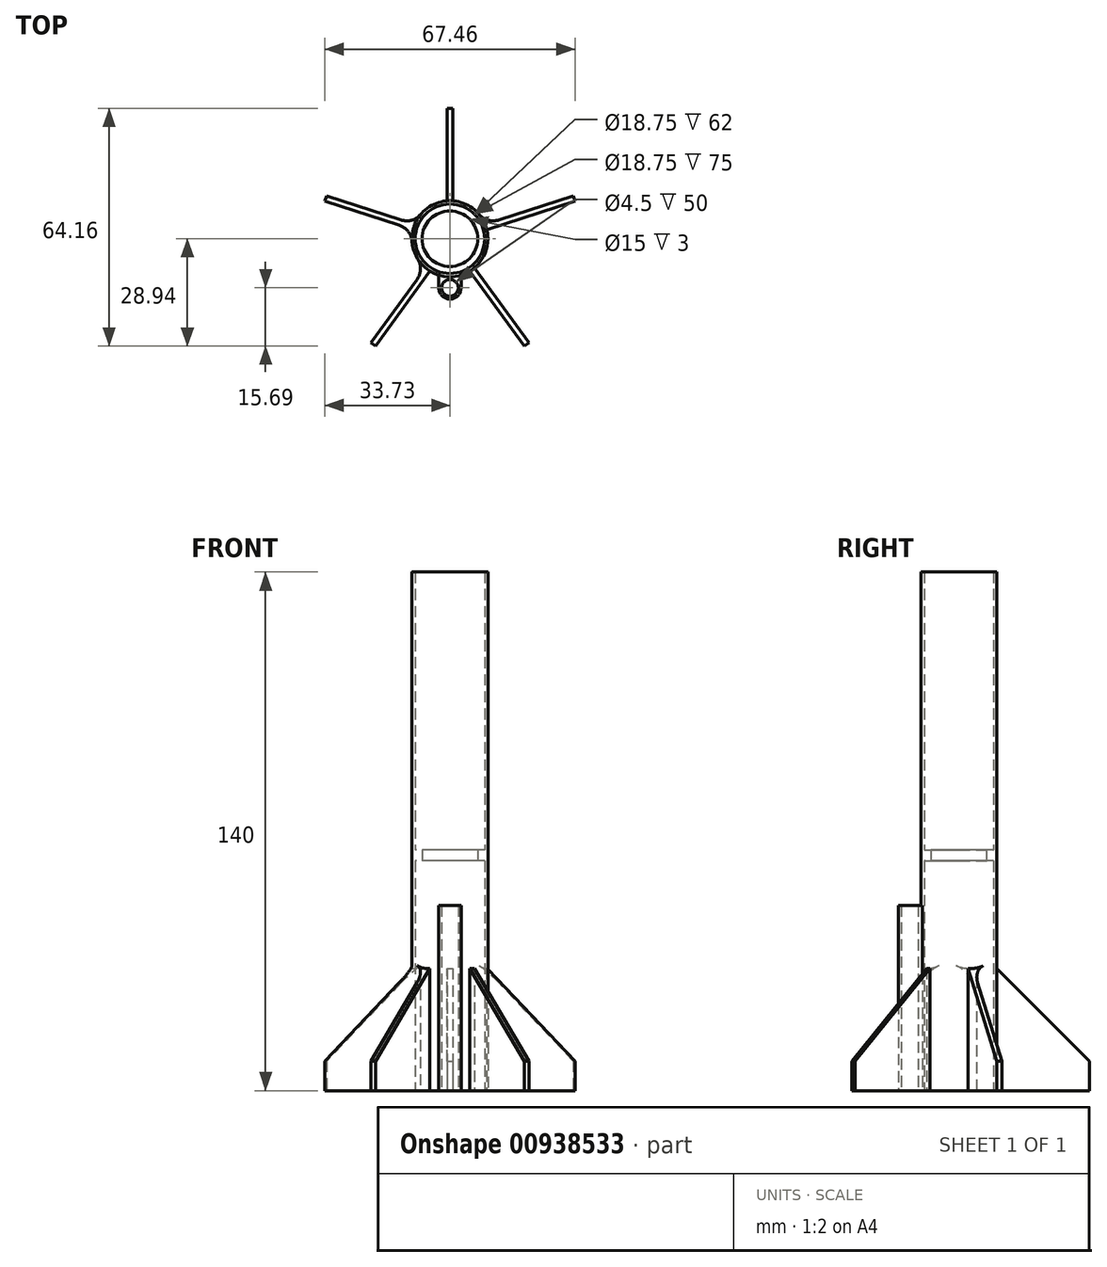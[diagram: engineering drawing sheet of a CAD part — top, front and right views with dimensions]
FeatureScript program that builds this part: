
annotation { "Feature Type Name" : "Feature", "Feature Type Description" : "" }
export const myFeature = defineFeature(function(context is Context, id is Id, definition is map)
    precondition{}
    {
        {
            var Q0;
            Q0=qCreatedBy(makeId("Top.planeOp"),FACE);
            var sketch = newSketch(context, id + "F0", { "sketchPlane" : qUnion([Q0])});
            skCircle(sketch, "E0", {"center": v(0, 0) * mm, "radius": 10.25 * mm});
            skCircle(sketch, "E1", {"center": v(0, 0) * mm, "radius": 9.38 * mm});
            skCircle(sketch, "E2", {"center": v(0, -13.25) * mm, "radius": 3 * mm});
            skCircle(sketch, "E3", {"center": v(0, -13.25) * mm, "radius": 2.25 * mm});
            skLineSegment(sketch, "E4", {"start": v(-3, -9.8) * mm, "end": v(-3, -13.25) * mm});
            skLineSegment(sketch, "E5.MirrorCS", {"start": v(3, -9.8) * mm, "end": v(3, -13.25) * mm});
            skLineSegment(sketch, "E6.bottom", {"start": v(-0.75, 35.22) * mm, "end": v(0.75, 35.22) * mm});
            skLineSegment(sketch, "E6.top", {"start": v(-0.75, 10.22) * mm, "end": v(0.75, 10.22) * mm, "construction": true});
            skLineSegment(sketch, "E6.left", {"start": v(-0.75, 35.22) * mm, "end": v(-0.75, 10.22) * mm});
            skLineSegment(sketch, "E6.right", {"start": v(0.75, 35.22) * mm, "end": v(0.75, 10.22) * mm});
            skCircle(sketch, "E7", {"center": v(0, 0) * mm, "radius": 7.5 * mm});
            skSolve(sketch);
        }
        {
            var Q0;
            Q0=makeQuery(id+"F0.imprint","IMPRINT",FACE,{"disambiguationData":[TD([[makeQuery(id+"F0.imprint","IMPRINT",EDGE,{"derivedFrom":sQuery(id+"F0.wireOp",EDGE,"E1")}),-1.0]])]});
            extrude(context, id + "F1", {"entities" : qUnion([Q0]), "depth" : 140 * mm, "offsetDistance" : 25 * mm});
        }
        {
            var Q0;
            Q0=makeQuery(id+"F0.imprint","IMPRINT",FACE,{"disambiguationData":[TD([[makeQuery(id+"F0.imprint","IMPRINT",EDGE,{"derivedFrom":sQuery(id+"F0.wireOp",EDGE,"E6.bottom")}),-1.0]])]});
            extrude(context, id + "F2", {"entities" : qUnion([Q0]), "operationType" : NewBodyOperationType.ADD, "depth" : 48 * mm, "offsetDistance" : 25 * mm});
        }
        {
            var Q0;
            Q0=makeQuery(id+"F2.opExtrude","CAP_EDGE",EDGE,{"disambiguationData":[OSD([sQuery(id+"F0.wireOp",EDGE,"E6.bottom")])],"isStart":false});
            chamfer(context, id + "F3", {"entities" : qUnion([Q0]), "width" : 40 * mm, "tangentPropagation" : true});
        }
        {
            var Q0;
            Q0=makeQuery(id+"F1.opExtrude","SWEPT_BODY",BODY,{"disambiguationData":[OSD([sQuery(id+"F0.wireOp",EDGE,"E0"),sQuery(id+"F0.wireOp",EDGE,"E1")])]});
            var Q1;
            Q1=sQuery(id+"F0.wireOp",EDGE,"E0");
            circularPattern(context, id + "F4", {"operationType" : NewBodyOperationType.ADD, "entities" : qUnion([Q0]), "axis" : qUnion([Q1]), "angle" : 360 * degree, "instanceCount" : 5, "equalSpace" : true});
        }
        {
            var Q0;
            Q0=makeQuery(id+"F0.imprint","IMPRINT",FACE,{"disambiguationData":[TD([[makeQuery(id+"F0.imprint","IMPRINT",EDGE,{"derivedFrom":sQuery(id+"F0.wireOp",EDGE,"E3")}),-1.0]])]});
            var Q1;
            {var subQ0=sQuery(id+"F0.wireOp",EDGE,"E5.MirrorCS");Q1=makeQuery(id+"F0.imprint","IMPRINT",FACE,{"disambiguationData":[TD([[makeQuery(id+"F0.imprint","IMPRINT",EDGE,{"derivedFrom":subQ0}),-1.0]])]});}
            var Q2;
            {var subQ0=sQuery(id+"F0.wireOp",EDGE,"E4");Q2=makeQuery(id+"F0.imprint","IMPRINT",FACE,{"disambiguationData":[TD([[makeQuery(id+"F0.imprint","IMPRINT",EDGE,{"derivedFrom":subQ0}),1.0]])]});}
            extrude(context, id + "F5", {"entities" : qUnion([Q0, Q1, Q2]), "operationType" : NewBodyOperationType.ADD, "depth" : 50 * mm, "offsetDistance" : 25 * mm});
        }
        {
            var Q0;
            Q0=makeQuery(id+"F0.imprint","IMPRINT",FACE,{"disambiguationData":[TD([[makeQuery(id+"F0.imprint","IMPRINT",EDGE,{"derivedFrom":sQuery(id+"F0.wireOp",EDGE,"E1")}),1.0]])]});
            var Q1;
            Q1=sQuery(id+"F0.wireOp",EDGE,"E7");
            extrude(context, id + "F6", {"entities" : qUnion([Q0]), "operationType" : NewBodyOperationType.ADD, "surfaceOperationType" : NewSurfaceOperationType.ADD, "surfaceEntities" : qUnion([Q1]), "depth" : 65 * mm, "offsetDistance" : 25 * mm, "hasSecondDirection" : true, "secondDirectionOppositeDirection" : false, "secondDirectionDepth" : 62 * mm});
        }
        {
            var Q0;
            {var subQ0=makeQuery(id+"F1.opExtrude","SWEPT_FACE",FACE,{"disambiguationData":[OSD([sQuery(id+"F0.wireOp",EDGE,"E0")])]});var subQ1=subQ0;Q0=makeQuery(id+"F4.boolean.opBoolean","INTERSECT",EDGE,{"disambiguationData":[topologyDisambiguationEdgeConnected([makeQuery(id+"F4.opPattern","COPY",FACE,{"derivedFrom":makeQuery(id+"F2.opExtrude","SWEPT_FACE",FACE,{"disambiguationData":[OSD([sQuery(id+"F0.wireOp",EDGE,"E6.left")])]}),"instanceName":"4"})])],"derivedFrom":[subQ1,makeQuery(id+"F4.opPattern","COPY",FACE,{"derivedFrom":subQ1,"instanceName":"1"}),makeQuery(id+"F4.opPattern","COPY",FACE,{"derivedFrom":subQ1,"instanceName":"2"}),makeQuery(id+"F4.opPattern","COPY",FACE,{"derivedFrom":subQ1,"instanceName":"3"})]});}
            var Q1;
            Q1=makeQuery(id+"F2.opExtrude","SWEPT_EDGE",EDGE,{"disambiguationData":[OSD([sQuery(id+"F0.wireOp",EDGE,"E0"),sQuery(id+"F0.wireOp",EDGE,"E6.right")])]});
            var Q2;
            Q2=makeQuery(id+"F2.opExtrude","SWEPT_EDGE",EDGE,{"disambiguationData":[OSD([sQuery(id+"F0.wireOp",EDGE,"E0"),sQuery(id+"F0.wireOp",EDGE,"E6.left")])]});
            var Q3;
            {var subQ0=makeQuery(id+"F1.opExtrude","SWEPT_FACE",FACE,{"disambiguationData":[OSD([sQuery(id+"F0.wireOp",EDGE,"E0")])]});var subQ1=subQ0;Q3=makeQuery(id+"F4.boolean.opBoolean","INTERSECT",EDGE,{"disambiguationData":[topologyDisambiguationEdgeConnected([makeQuery(id+"F4.opPattern","COPY",FACE,{"derivedFrom":makeQuery(id+"F2.opExtrude","SWEPT_FACE",FACE,{"disambiguationData":[OSD([sQuery(id+"F0.wireOp",EDGE,"E6.right")])]}),"instanceName":"1"})])],"derivedFrom":[subQ1,makeQuery(id+"F4.opPattern","COPY",FACE,{"derivedFrom":subQ1,"instanceName":"2"})]});}
            var Q4;
            {var subQ0=makeQuery(id+"F1.opExtrude","SWEPT_FACE",FACE,{"disambiguationData":[OSD([sQuery(id+"F0.wireOp",EDGE,"E0")])]});var subQ1=subQ0;Q4=makeQuery(id+"F4.boolean.opBoolean","INTERSECT",EDGE,{"disambiguationData":[topologyDisambiguationEdgeConnected([makeQuery(id+"F4.opPattern","COPY",FACE,{"derivedFrom":makeQuery(id+"F2.opExtrude","SWEPT_FACE",FACE,{"disambiguationData":[OSD([sQuery(id+"F0.wireOp",EDGE,"E6.left")])]}),"instanceName":"1"})])],"derivedFrom":[subQ1,makeQuery(id+"F4.opPattern","COPY",FACE,{"derivedFrom":subQ1,"instanceName":"2"})]});}
            var Q5;
            {var subQ0=makeQuery(id+"F1.opExtrude","SWEPT_FACE",FACE,{"disambiguationData":[OSD([sQuery(id+"F0.wireOp",EDGE,"E0")])]});var subQ1=subQ0;Q5=makeQuery(id+"F4.boolean.opBoolean","INTERSECT",EDGE,{"disambiguationData":[topologyDisambiguationEdgeConnected([makeQuery(id+"F4.opPattern","COPY",FACE,{"derivedFrom":makeQuery(id+"F2.opExtrude","SWEPT_FACE",FACE,{"disambiguationData":[OSD([sQuery(id+"F0.wireOp",EDGE,"E6.right")])]}),"instanceName":"2"})])],"derivedFrom":[subQ1,makeQuery(id+"F4.opPattern","COPY",FACE,{"derivedFrom":subQ1,"instanceName":"1"}),makeQuery(id+"F4.opPattern","COPY",FACE,{"derivedFrom":subQ1,"instanceName":"3"})]});}
            fillet(context, id + "F7", {"entities" : qUnion([Q0, Q1, Q2, Q3, Q4, Q5]), "radius" : 5 * mm, "tangentPropagation" : true, "allowEdgeOverflow" : false});
        }
    });
